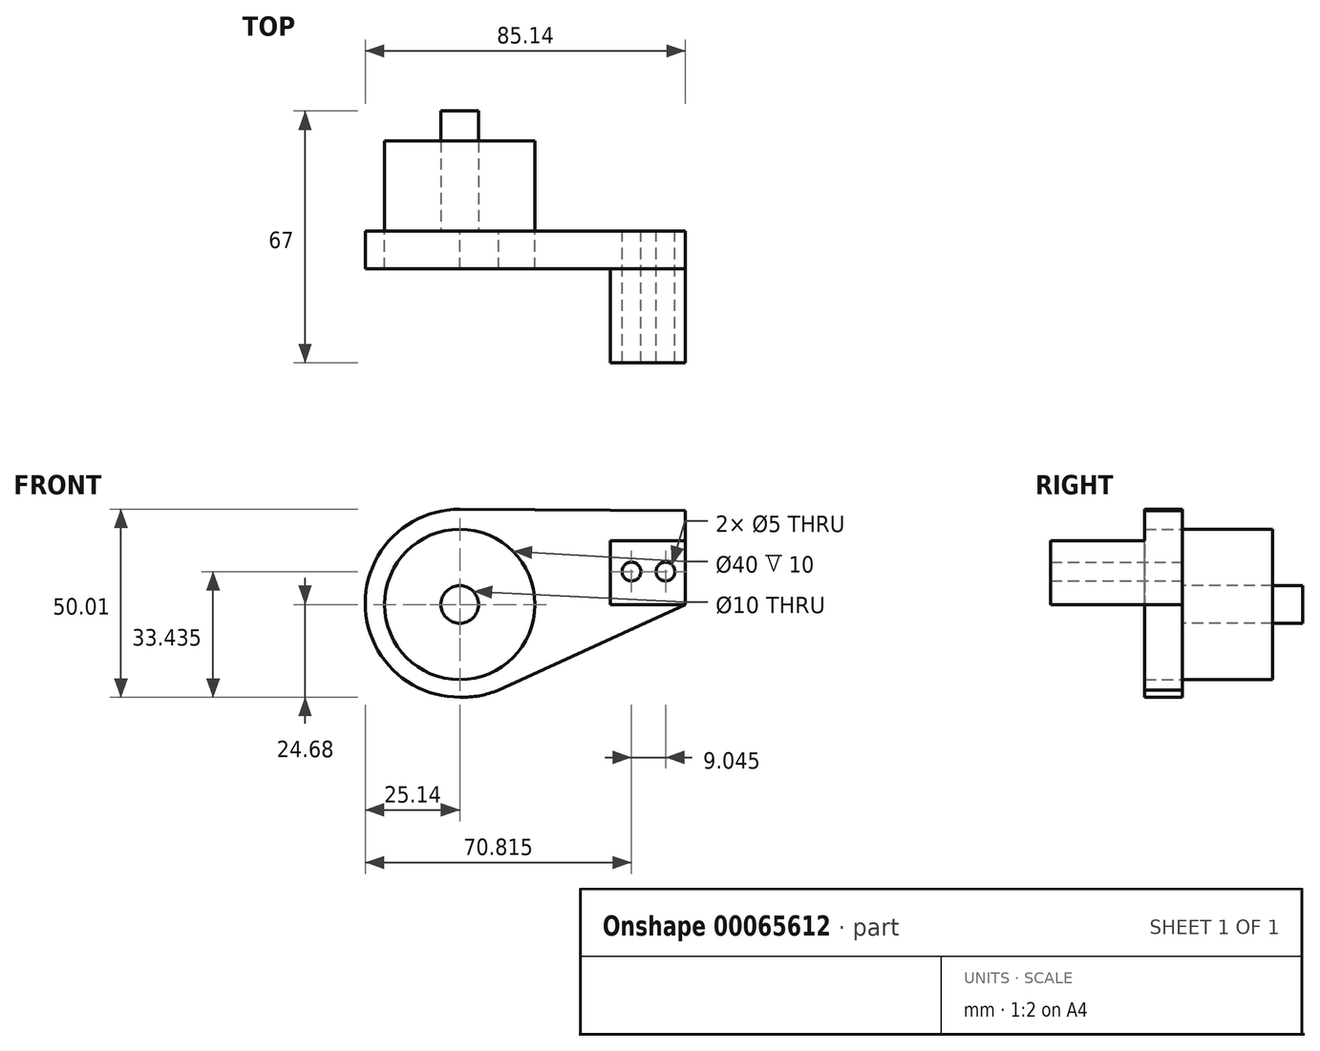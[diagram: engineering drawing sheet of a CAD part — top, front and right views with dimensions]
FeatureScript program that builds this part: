
annotation { "Feature Type Name" : "Feature", "Feature Type Description" : "" }
export const myFeature = defineFeature(function(context is Context, id is Id, definition is map)
    precondition{}
    {
        {
            var Q0;
            Q0=qCreatedBy(makeId("Front.planeOp"),FACE);
            var sketch = newSketch(context, id + "F0", { "sketchPlane" : qUnion([Q0])});
            skCircle(sketch, "E0", {"center": v(0, 0) * mm, "radius": 5 * mm});
            skCircle(sketch, "E1", {"center": v(0, 0) * mm, "radius": 10 * mm, "construction": true});
            skCircle(sketch, "E2", {"center": v(0, 0) * mm, "radius": 17.5 * mm, "construction": true});
            skCircle(sketch, "E3", {"center": v(0, 0) * mm, "radius": 20 * mm});
            skCircle(sketch, "E4", {"center": v(0, 0) * mm, "radius": 21 * mm, "construction": true});
            skArc(sketch, "E5", {"start": v(0, 25.33) * mm, "mid": v(-25.14, 0.33) * mm, "end": v(0, -24.67) * mm});
            skArc(sketch, "E6", {"start": v(0, -24.67) * mm, "mid": v(5.25, -24.27) * mm, "end": v(10.3, -22.78) * mm});
            skLineSegment(sketch, "E7", {"start": v(10.3, -22.78) * mm, "end": v(60, 0) * mm});
            skLineSegment(sketch, "E8", {"start": v(40, 0) * mm, "end": v(40, 25.1) * mm});
            skLineSegment(sketch, "E9", {"start": v(0, 25.33) * mm, "end": v(40, 25.1) * mm});
            skLineSegment(sketch, "E10", {"start": v(40, 25.1) * mm, "end": v(60, 25) * mm});
            skLineSegment(sketch, "E11", {"start": v(60, 25) * mm, "end": v(60, 0) * mm});
            skLineSegment(sketch, "E12", {"start": v(60, 0) * mm, "end": v(40, 0) * mm});
            skLineSegment(sketch, "E13", {"start": v(60, 0) * mm, "end": v(60, 17) * mm});
            skLineSegment(sketch, "E14", {"start": v(60, 17) * mm, "end": v(40, 17) * mm});
            skCircle(sketch, "E15", {"center": v(54.72, 8.76) * mm, "radius": 2.5 * mm});
            skCircle(sketch, "E16", {"center": v(45.68, 8.76) * mm, "radius": 2.5 * mm});
            skSolve(sketch);
        }
        {
            var Q0;
            Q0=makeQuery(id+"F0.imprint","IMPRINT",FACE,{"disambiguationData":[TD([[makeQuery(id+"F0.imprint","IMPRINT",EDGE,{"derivedFrom":sQuery(id+"F0.wireOp",EDGE,"E0")}),-1.0]])]});
            extrude(context, id + "F1", {"entities" : qUnion([Q0]), "oppositeDirection" : true, "depth" : 24 * mm});
        }
        {
            var Q0;
            Q0=makeQuery(id+"F0.imprint","IMPRINT",FACE,{"disambiguationData":[TD([[makeQuery(id+"F0.imprint","IMPRINT",EDGE,{"derivedFrom":sQuery(id+"F0.wireOp",EDGE,"E3")}),-1.0]])]});
            extrude(context, id + "F2", {"entities" : qUnion([Q0]), "depth" : 10 * mm});
        }
        {
            var Q0;
            {var subQ1=sQuery(id+"F0.wireOp",EDGE,"E12");Q0=makeQuery(id+"F0.imprint","IMPRINT",FACE,{"disambiguationData":[TD([[makeQuery(id+"F0.imprint","IMPRINT",EDGE,{"derivedFrom":subQ1}),-1.0]])]});}
            extrude(context, id + "F3", {"entities" : qUnion([Q0]), "operationType" : NewBodyOperationType.ADD, "depth" : 35 * mm});
        }
        {
            var Q0;
            {var subQ0=sQuery(id+"F0.wireOp",EDGE,"E10");Q0=makeQuery(id+"F0.imprint","IMPRINT",FACE,{"disambiguationData":[TD([[makeQuery(id+"F0.imprint","IMPRINT",EDGE,{"derivedFrom":subQ0}),-1.0]])]});}
            extrude(context, id + "F4", {"entities" : qUnion([Q0]), "operationType" : NewBodyOperationType.ADD, "depth" : 10 * mm});
        }
        {
            var Q0;
            Q0=makeQuery(id+"F0.imprint","IMPRINT",FACE,{"disambiguationData":[TD([[makeQuery(id+"F0.imprint","IMPRINT",EDGE,{"derivedFrom":sQuery(id+"F0.wireOp",EDGE,"E0")}),1.0]])]});
            extrude(context, id + "F5", {"entities" : qUnion([Q0]), "oppositeDirection" : true, "depth" : 32 * mm});
        }
    });
